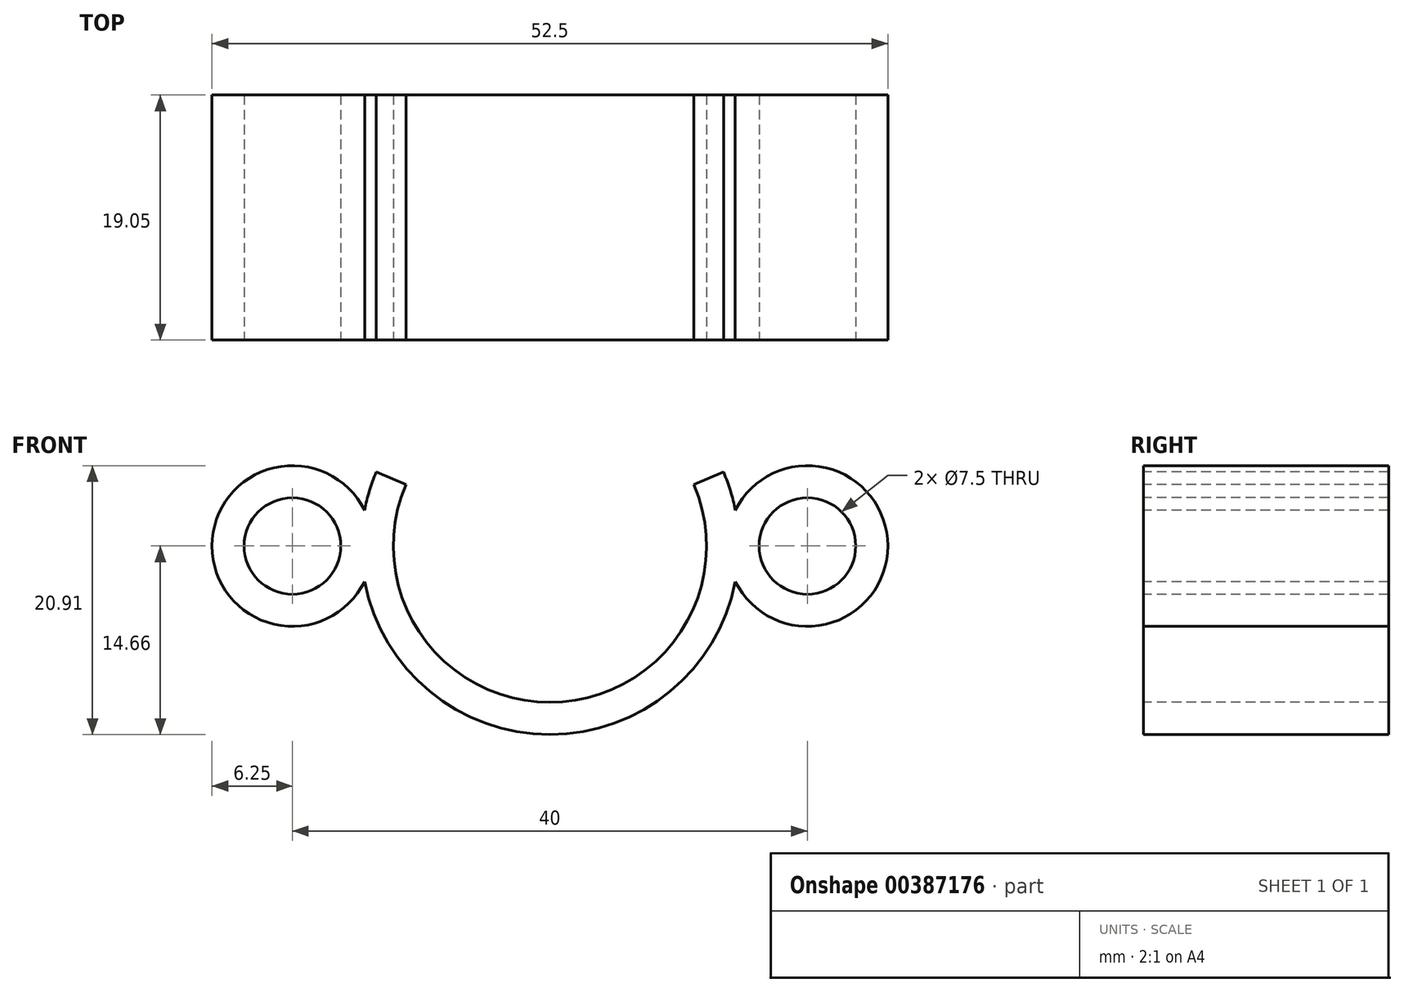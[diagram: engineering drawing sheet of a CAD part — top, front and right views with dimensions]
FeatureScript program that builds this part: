
annotation { "Feature Type Name" : "Feature", "Feature Type Description" : "" }
export const myFeature = defineFeature(function(context is Context, id is Id, definition is map)
    precondition{}
    {
        {
            var Q0;
            Q0=qCreatedBy(makeId("Front.planeOp"),FACE);
            var sketch = newSketch(context, id + "F0", { "sketchPlane" : qUnion([Q0])});
            skArc(sketch, "E0", {"start": v(-11.19, 4.77) * mm, "mid": v(0, -12.16) * mm, "end": v(11.19, 4.77) * mm});
            skCircle(sketch, "E1", {"center": v(20, 0) * mm, "radius": 3.75 * mm});
            skCircle(sketch, "E2", {"center": v(-20, 0) * mm, "radius": 3.75 * mm});
            skLineSegment(sketch, "E3", {"start": v(-20, 0) * mm, "end": v(0, 0) * mm, "construction": true});
            skLineSegment(sketch, "E4", {"start": v(20, 0) * mm, "end": v(0, 0) * mm, "construction": true});
            skArc(sketch, "E5", {"start": v(-14.4, 2.77) * mm, "mid": v(-26.25, 0) * mm, "end": v(-14.4, -2.77) * mm});
            skArc(sketch, "E6", {"start": v(-14.4, -2.77) * mm, "mid": v(0, -14.66) * mm, "end": v(14.4, -2.77) * mm});
            skArc(sketch, "E7", {"start": v(14.4, -2.77) * mm, "mid": v(26.25, 0) * mm, "end": v(14.4, 2.77) * mm});
            skArc(sketch, "E8.trimOffspring", {"start": v(14.4, 2.77) * mm, "mid": v(14.02, 4.28) * mm, "end": v(13.49, 5.74) * mm});
            skLineSegment(sketch, "E9", {"start": v(-11.19, 4.77) * mm, "end": v(-13.49, 5.74) * mm});
            skLineSegment(sketch, "E10", {"start": v(13.49, 5.74) * mm, "end": v(11.19, 4.77) * mm});
            skArc(sketch, "E11.trimOffspring", {"start": v(-13.49, 5.74) * mm, "mid": v(-14.02, 4.28) * mm, "end": v(-14.4, 2.77) * mm});
            skLineSegment(sketch, "E12", {"start": v(-11.19, 4.77) * mm, "end": v(-14.4, -2.77) * mm, "construction": true});
            skSolve(sketch);
        }
        {
            var Q0;
            Q0=makeQuery(id+"F0.imprint","IMPRINT",FACE,{"disambiguationData":[TD([[makeQuery(id+"F0.imprint","IMPRINT",EDGE,{"derivedFrom":sQuery(id+"F0.wireOp",EDGE,"E0")}),-1.0]])]});
            extrude(context, id + "F1", {"entities" : qUnion([Q0]), "oppositeDirection" : true, "offsetDistance" : 25 * mm, "depth" : 19.05 * mm});
        }
    });
